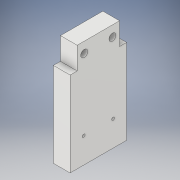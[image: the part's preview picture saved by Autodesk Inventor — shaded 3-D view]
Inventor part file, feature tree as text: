
AUTODESK INVENTOR PART (.ipt)
format: ipt  version: 2017 (Build 210142000, 142)  size: 133,632 bytes
history: native  units: in
note: dims shown in document units (in); Inventor stores cm internally (conversion verified against a paired STEP export)
features: extrude x2, sketch x2, projected_geometry x1
ambient origin geometry x8: Origin, YZ Plane, XZ Plane, XY Plane, X Axis, Y Axis, Z Axis, Center Point
bodies: Solid1 (feature_tree)
feature tree (5):
  extrude  "Extrusion1"  Depth=1.0in
  extrude  "Extrusion2"  Depth=0.75in
  sketch  "Sketch1"  dims[d1=1.0in d2=0.25in]
  sketch  "Sketch2"  dims[d3=0.25in d6=0.75in d7=0.74in d8=0.7in d9=0.07in d10=0.09in d11=0.05in d12=0.2953in d13=0.0in d14=0.75in d15=0.2953in d16=0.0in d18=0.188in d19=0.125in]
  projected_geometry  "Projected Loop1"
